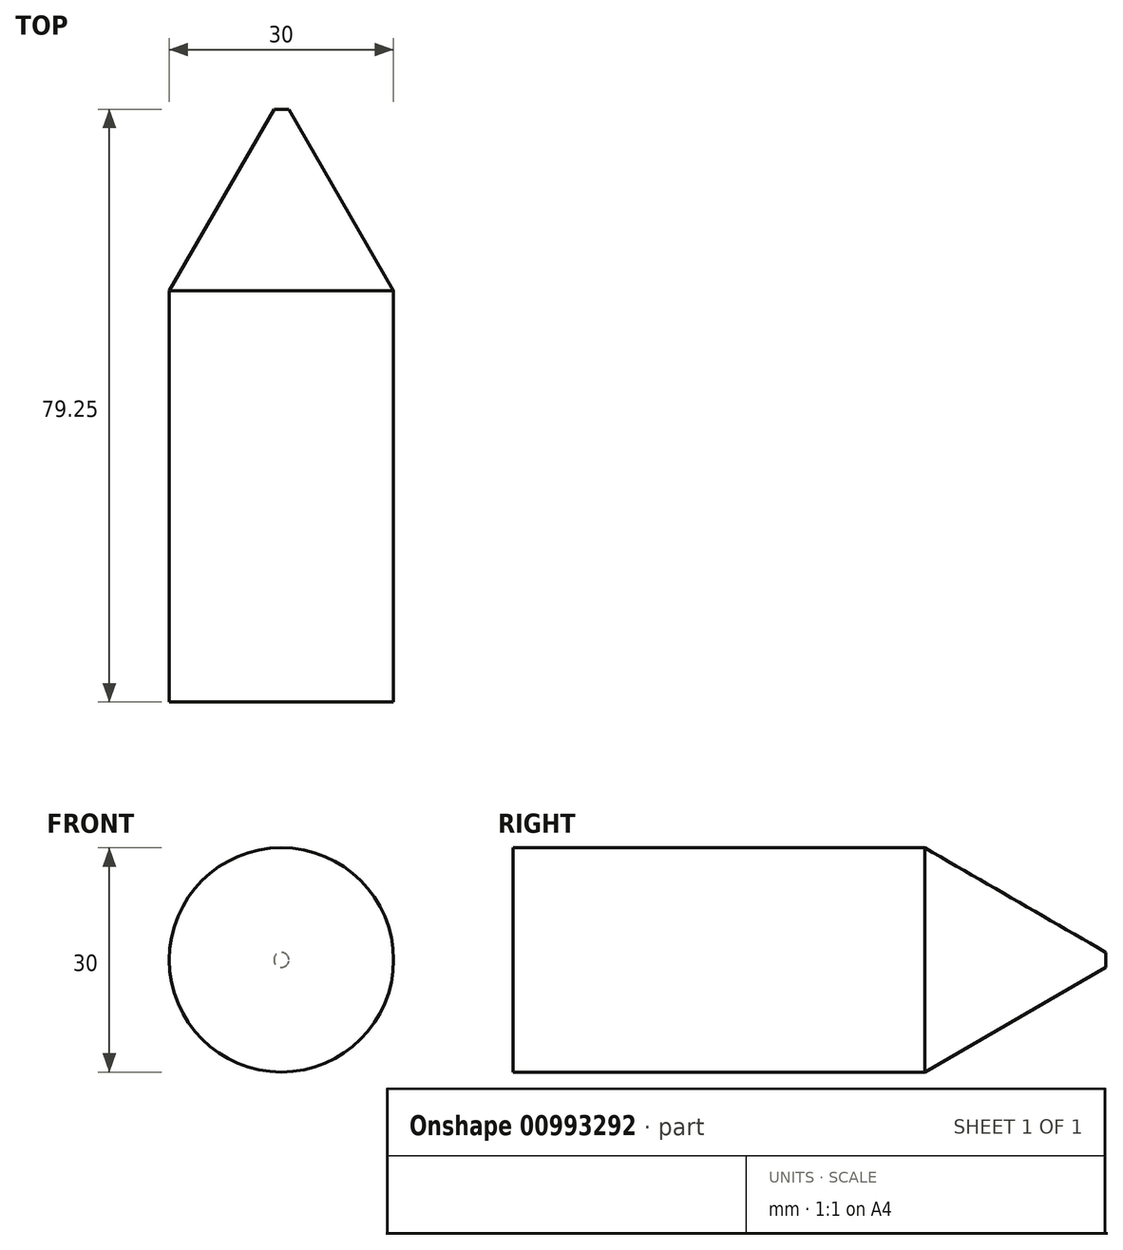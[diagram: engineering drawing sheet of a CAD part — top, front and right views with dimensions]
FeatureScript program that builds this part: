
annotation { "Feature Type Name" : "Feature", "Feature Type Description" : "" }
export const myFeature = defineFeature(function(context is Context, id is Id, definition is map)
    precondition{}
    {
        {
            var Q0;
            Q0=qCreatedBy(makeId("Top.planeOp"),FACE);
            var sketch = newSketch(context, id + "F0", { "sketchPlane" : qUnion([Q0])});
            skLineSegment(sketch, "E0.bottom", {"start": v(-15, 35.36) * mm, "end": v(15, 35.36) * mm});
            skLineSegment(sketch, "E0.top", {"start": v(-15, -19.64) * mm, "end": v(15, -19.64) * mm});
            skLineSegment(sketch, "E0.left", {"start": v(-15, 35.36) * mm, "end": v(-15, -19.64) * mm});
            skLineSegment(sketch, "E0.right", {"start": v(15, 35.36) * mm, "end": v(15, -19.64) * mm});
            skLineSegment(sketch, "E1", {"start": v(0, 61.34) * mm, "end": v(-15, 35.36) * mm});
            skLineSegment(sketch, "E2", {"start": v(0, 61.34) * mm, "end": v(15, 35.36) * mm});
            skLineSegment(sketch, "E3", {"start": v(-1, 59.6) * mm, "end": v(1, 59.6) * mm});
            skLineSegment(sketch, "E4", {"start": v(0, 59.6) * mm, "end": v(0, -19.64) * mm});
            skSolve(sketch);
        }
        {
            var Q0;
            {var subQ0=sQuery(id+"F0.wireOp",EDGE,"E1");var subQ5=sQuery(id+"F0.wireOp",EDGE,"E3");var subQ6=makeQuery(id+"F0.imprint","INTERSECT",VERTEX,{"derivedFrom":[subQ0,subQ5]});Q0=makeQuery(id+"F0.imprint","IMPRINT",FACE,{"disambiguationData":[TD([[makeQuery(id+"F0.imprint","IMPRINT",EDGE,{"disambiguationData":[TD([[subQ6,-1.0]])],"derivedFrom":subQ5}),-1.0]])]});}
            var Q1;
            {var subQ0=sQuery(id+"F0.wireOp",EDGE,"E0.left");Q1=makeQuery(id+"F0.imprint","IMPRINT",FACE,{"disambiguationData":[TD([[makeQuery(id+"F0.imprint","IMPRINT",EDGE,{"derivedFrom":subQ0}),1.0]])]});}
            var Q2;
            Q2=sQuery(id+"F0.wireOp",EDGE,"E4");
            revolve(context, id + "F1", {"surfaceOperationType" : NewSurfaceOperationType.NEW, "entities" : qUnion([Q0, Q1]), "axis" : qUnion([Q2]), "revolveType" : RevolveType.FULL});
        }
    });
